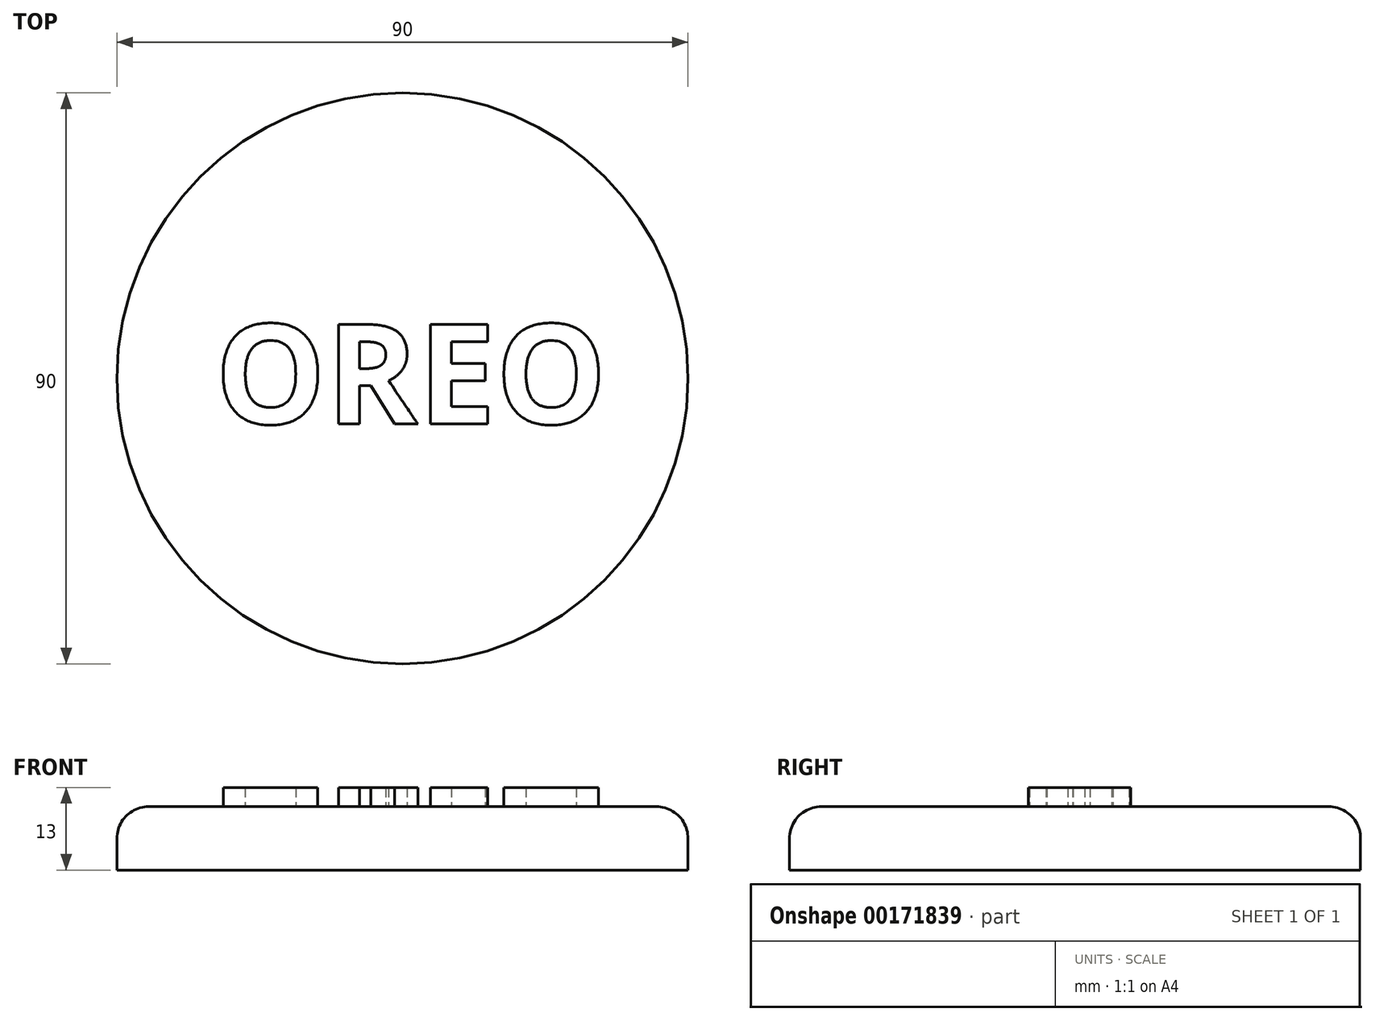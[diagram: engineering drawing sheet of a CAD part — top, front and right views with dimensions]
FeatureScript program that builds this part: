
annotation { "Feature Type Name" : "Feature", "Feature Type Description" : "" }
export const myFeature = defineFeature(function(context is Context, id is Id, definition is map)
    precondition{}
    {
        {
            var Q0;
            Q0=qCreatedBy(makeId("Top.planeOp"),FACE);
            var sketch = newSketch(context, id + "F0", { "sketchPlane" : qUnion([Q0])});
            skCircle(sketch, "E0", {"center": v(0, 0) * mm, "radius": 45 * mm});
            skSolve(sketch);
        }
        {
            var Q0;
            Q0 = qSketchRegion(id + "F0", true);
            extrude(context, id + "F1", {"entities" : qUnion([Q0]), "oppositeDirection" : true, "depth" : 10 * mm});
        }
        {
            var Q0;
            Q0=makeQuery(id+"F1.opExtrude","CAP_FACE",FACE,{"disambiguationData":[OSD([sQuery(id+"F0.wireOp",EDGE,"E0")])],"isStart":true});
            fillet(context, id + "F2", {"entities" : qUnion([Q0]), "radius" : 5 * mm, "tangentPropagation" : true, "allowEdgeOverflow" : false});
        }
        {
            var Q0;
            Q0=makeQuery(id+"F1.opExtrude","CAP_FACE",FACE,{"disambiguationData":[OSD([sQuery(id+"F0.wireOp",EDGE,"E0")])],"isStart":true});
            var sketch = newSketch(context, id + "F3", { "sketchPlane" : qUnion([Q0])});
            skText(sketch, "E1", { "text": "OREO\n", "fontName": "OpenSans-Bold.ttf"});
            const initialGuessF3  = {"E1": [-0.02953, -0.00716, 1, 0, 0.0158]};
            skSetInitialGuess(sketch, initialGuessF3);
            skSolve(sketch);
        }
        {
            var Q0;
            Q0 = qSketchRegion(id + "F3", true);
            extrude(context, id + "F4", {"entities" : qUnion([Q0]), "operationType" : NewBodyOperationType.ADD, "depth" : 3 * mm});
        }
    });
